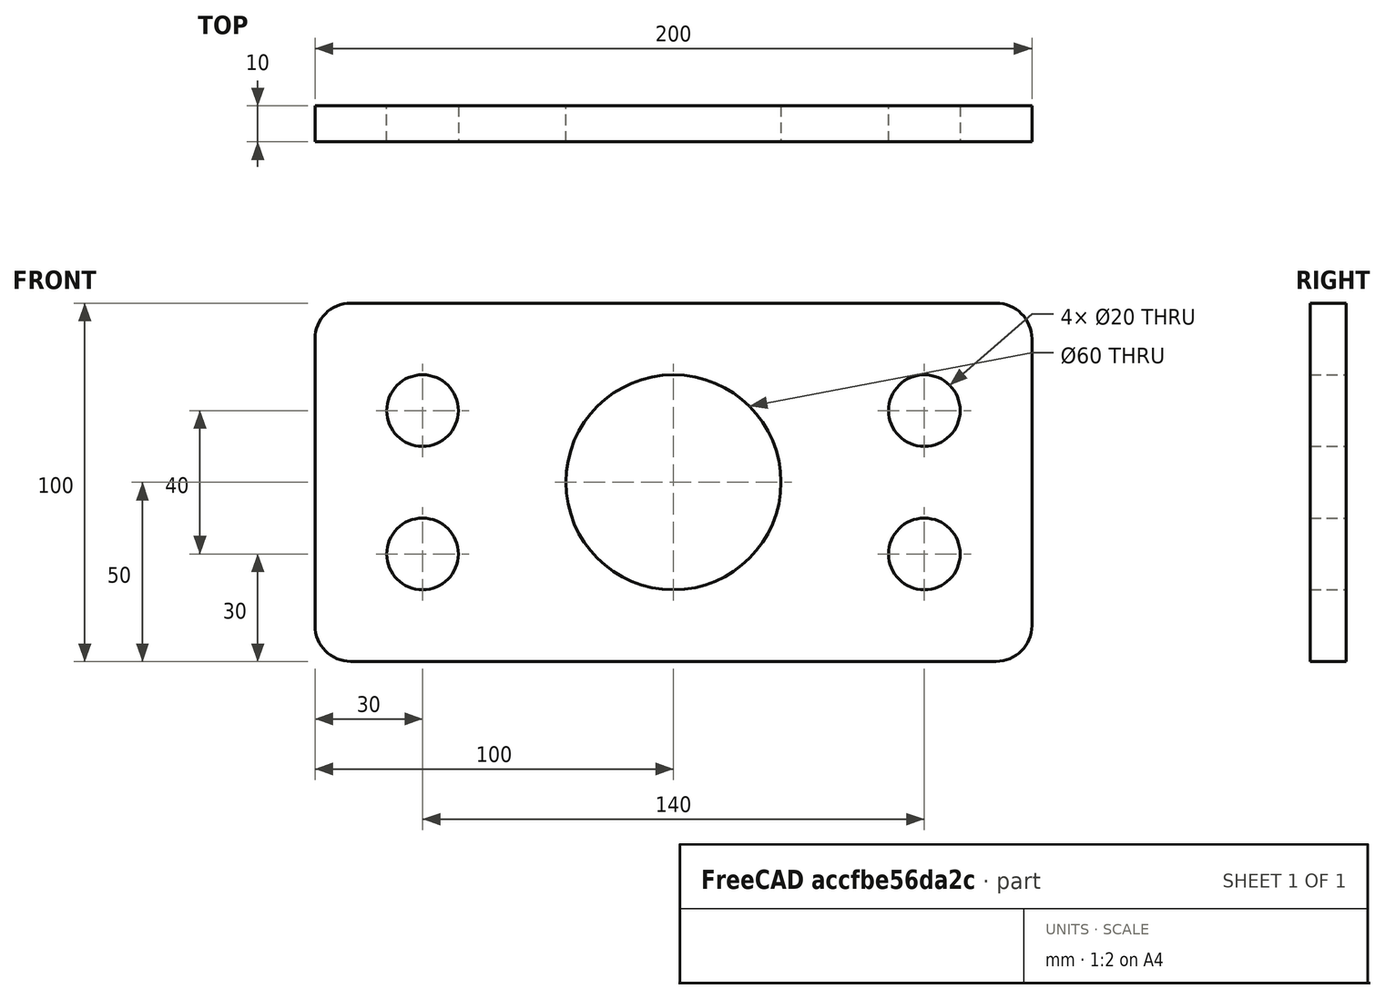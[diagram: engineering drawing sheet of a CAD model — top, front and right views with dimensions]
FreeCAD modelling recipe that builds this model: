
FCSTD DOCUMENT  (FreeCAD 0.18R4 (GitTag))
Label: Assignment-2
License: All rights reserved
LicenseURL: http://en.wikipedia.org/wiki/All_rights_reserved
objects: TechDraw::DrawViewDimension×8, TechDraw::DrawViewAnnotation×4, TechDraw::DrawViewPart×3, PartDesign::Fillet×2, Sketcher::SketchObject×1, PartDesign::Pad×1, PartDesign::Body×1, TechDraw::DrawSVGTemplate×1, TechDraw::DrawPage×1
note: 6 computed .brp shape members not serialized (recipe doc carries the construction recipe); baked Part::Feature solids carry a one-line shape summary decoded from their .brp

FEATURE [Sketcher::SketchObject] Sketch
  MapMode = 5
  Placement = pos=(0,0,0) rot=(1,0,0;1.5708rad)
  Support = -> [XZ_Plane]
  sketch-geometry (9):
    g0: LineSegment StartX=-100 StartY=50 StartZ=0 EndX=100 EndY=50 EndZ=0
    g1: LineSegment StartX=100 StartY=50 StartZ=0 EndX=100 EndY=-50 EndZ=0
    g2: LineSegment StartX=100 StartY=-50 StartZ=0 EndX=-100 EndY=-50 EndZ=0
    g3: LineSegment StartX=-100 StartY=-50 StartZ=0 EndX=-100 EndY=50 EndZ=0
    g4: Circle CenterX=0 CenterY=0 CenterZ=0 NormalX=0 NormalY=0 NormalZ=1 AngleXU=0 Radius=30
    g5: Circle CenterX=-70 CenterY=20 CenterZ=0 NormalX=0 NormalY=0 NormalZ=1 AngleXU=0 Radius=10
    g6: Circle CenterX=70 CenterY=20 CenterZ=0 NormalX=0 NormalY=0 NormalZ=1 AngleXU=0 Radius=10
    g7: Circle CenterX=70 CenterY=-20 CenterZ=0 NormalX=0 NormalY=0 NormalZ=1 AngleXU=0 Radius=10
    g8: Circle CenterX=-70 CenterY=-20 CenterZ=0 NormalX=0 NormalY=0 NormalZ=1 AngleXU=0 Radius=10
  constraints (25):
    c: Coincident(g0,g1)
    c: Coincident(g1,g2)
    c: Coincident(g2,g3)
    c: Coincident(g3,g0)
    c: Horizontal(g0)
    c: Horizontal(g2)
    c: Vertical(g1)
    c: Vertical(g3)
    c: Symmetric(g1,g0,g-1)
    c: DistanceX(g0,g0) = 200
    c: DistanceY(g3,g3) = 100
    c: Diameter(g4) = 60
    c: Coincident(g4,g-1)
    c: Radius(g5) = 10
    c: DistanceY(g-1,g5) = 20
    c: DistanceX(g5,g-1) = 70
    c: Radius(g6) = 10
    c: DistanceY(g-1,g6) = 20
    c: DistanceX(g-1,g6) = 70
    c: Radius(g8) = 10
    c: Radius(g7) = 10
    c: DistanceY(g8,g-1) = 20
    c: DistanceY(g7,g-1) = 20
    c: DistanceX(g8,g-1) = 70
    c: DistanceX(g-1,g7) = 70
FEATURE [PartDesign::Pad] Pad
  Length = 10
  Length2 = 100
  Placement = pos=(0,0,0) rot=(1,0,0;1.5708rad)
  Profile = -> Sketch
  Type = 0
FEATURE [PartDesign::Fillet] Fillet
  Base = -> Pad [Edge5,Edge2,Edge1]
  BaseFeature = -> Pad
  Placement = pos=(0,0,0) rot=(1,0,0;1.5708rad)
  Radius = 10
FEATURE [PartDesign::Fillet] Fillet001
  Base = -> Fillet [Edge29]
  BaseFeature = -> Fillet
  Placement = pos=(0,0,0) rot=(1,0,0;1.5708rad)
  Radius = 10
FEATURE [PartDesign::Body] Body
  Group = -> [Sketch,Pad,Fillet,Fillet001]
  Origin = -> Origin
  Tip = -> Fillet001
FEATURE [TechDraw::DrawSVGTemplate] Template
  EditableTexts = Designed_by_Name=SOUMOJIT SHOME; Drawing_number=Drawing number-01; FC-Date=08/11/2022; FC-SC=1:2; FC-SH=01; FC-Title=Academy of Technology; Subtitle=ECE-3 (X) ROLL-139; Weight=Weight
  Height = 210
  Orientation = 1
  Width = 297
FEATURE [TechDraw::DrawViewPart] View
  CoarseView = false
  Direction = (0,-1,0)
  Focus = 100
  HardHidden = false
  IsoCount = 0
  IsoHidden = false
  IsoVisible = false
  LockPosition = false
  Perspective = false
  Rotation = 0
  Scale = 0.5
  ScaleType = 0
  SeamHidden = false
  SeamVisible = false
  SmoothHidden = false
  SmoothVisible = false
  Source = -> [Fillet001]
  X = 93.3024
  Y = 148.577
FEATURE [TechDraw::DrawViewPart] View001
  CoarseView = false
  Direction = (0,0,1)
  Focus = 100
  HardHidden = false
  IsoCount = 0
  IsoHidden = false
  IsoVisible = false
  LockPosition = true
  Perspective = false
  Rotation = 0
  Scale = 0.5
  ScaleType = 0
  SeamHidden = false
  SeamVisible = false
  SmoothHidden = false
  SmoothVisible = false
  Source = -> [Fillet001]
  X = 79.3389
  Y = 61.8996
FEATURE [TechDraw::DrawViewPart] View002
  CoarseView = false
  Direction = (0.577,-0.577,0.577)
  Focus = 100
  HardHidden = false
  IsoCount = 0
  IsoHidden = false
  IsoVisible = false
  LockPosition = true
  Perspective = false
  Rotation = 0
  Scale = 0.5
  ScaleType = 0
  SeamHidden = false
  SeamVisible = false
  SmoothHidden = false
  SmoothVisible = false
  Source = -> [Fillet001]
  X = 224.449
  Y = 132.806
FEATURE [TechDraw::DrawViewAnnotation] Annotation
  Font = osifont
  LineSpace = 80
  LockPosition = false
  MaxWidth = -1
  Rotation = 0
  ScaleType = 0
  Text = Front View
  TextSize = 5
  TextStyle = 0
  X = 92.6833
  Y = 85.6386
FEATURE [TechDraw::DrawViewAnnotation] Annotation001
  Font = osifont
  LineSpace = 80
  LockPosition = false
  MaxWidth = -1
  Rotation = 0
  ScaleType = 0
  Text = Top View
  TextSize = 5
  TextStyle = 0
  X = 81.751
  Y = 44.9605
FEATURE [TechDraw::DrawViewAnnotation] Annotation002
  Font = osifont
  LineSpace = 80
  LockPosition = false
  MaxWidth = -1
  Rotation = 0
  ScaleType = 0
  Text = Isometric View
  TextSize = 5
  TextStyle = 0
  X = 216.771
  Y = 81.8294
FEATURE [TechDraw::DrawViewDimension] Dimension002
  Arbitrary = false
  FormatSpec = %.2f
  LockPosition = false
  MeasureType = 1
  OverTolerance = 0
  References2D = -> [View]
  Rotation = 0
  ScaleType = 0
  Type = 2
  UnderTolerance = 0
  X = 70.9026
  Y = 8.73322
FEATURE [TechDraw::DrawViewDimension] Dimension003
  Arbitrary = false
  FormatSpec = %.2f
  LockPosition = false
  MeasureType = 1
  OverTolerance = 0
  References2D = -> [View]
  Rotation = 0
  ScaleType = 0
  Type = 2
  UnderTolerance = 0
  X = -68.9054
  Y = 7.09095
FEATURE [TechDraw::DrawViewDimension] Dimension004
  Arbitrary = false
  FormatSpec = %.2f
  LockPosition = true
  MeasureType = 1
  OverTolerance = 0
  References2D = -> [View]
  Rotation = 0
  ScaleType = 0
  Type = 1
  UnderTolerance = 0
  X = -17.6294
  Y = -40.2197
FEATURE [TechDraw::DrawViewDimension] Dimension005
  Arbitrary = false
  FormatSpec = %.2f
  LockPosition = false
  MeasureType = 1
  OverTolerance = 0
  References2D = -> [View]
  Rotation = 0
  ScaleType = 0
  Type = 1
  UnderTolerance = 0
  X = 18.1794
  Y = -50.9505
FEATURE [TechDraw::DrawViewDimension] Dimension006
  Arbitrary = false
  FormatSpec = %.2f
  LockPosition = false
  MeasureType = 1
  OverTolerance = 0
  References2D = -> [View001]
  Rotation = 0
  ScaleType = 0
  Type = 2
  UnderTolerance = 0
  X = 54.8501
  Y = 14.0264
FEATURE [TechDraw::DrawViewAnnotation] Annotation003
  Font = osifont
  LineSpace = 80
  LockPosition = true
  MaxWidth = -1
  Rotation = 0
  ScaleType = 0
  Text = DRILL TEMPLATE
  TextSize = 5
  TextStyle = 0
  X = 211.716
  Y = 31.004
FEATURE [TechDraw::DrawViewDimension] Dimension008
  Arbitrary = false
  FormatSpec = R%.2f
  LockPosition = false
  MeasureType = 1
  OverTolerance = 0
  References2D = -> [View]
  Rotation = 0
  ScaleType = 0
  Type = 4
  UnderTolerance = 0
  X = 49.3874
  Y = 42.747
FEATURE [TechDraw::DrawViewDimension] Dimension
  Arbitrary = false
  FormatSpec = R%.2f
  LockPosition = false
  MeasureType = 1
  OverTolerance = 0
  References2D = -> [View]
  Rotation = 0
  ScaleType = 0
  Type = 4
  UnderTolerance = 0
  X = 75.9486
  Y = 30.2964
FEATURE [TechDraw::DrawViewDimension] Dimension009
  Arbitrary = false
  FormatSpec = R%.2f
  LockPosition = false
  MeasureType = 1
  OverTolerance = 0
  References2D = -> [View]
  Rotation = 0
  ScaleType = 0
  Type = 4
  UnderTolerance = 0
  X = -4.56522
  Y = 39.4269
FEATURE [TechDraw::DrawPage] Page
  KeepUpdated = true
  ProjectionType = 0
  Template = -> Template
  Views = -> [View,View001,View002,Annotation,Annotation001,Annotation002,Dimension002,Dimension003,Dimension004,Dimension005,Dimension006,Annotation003,Dimension008,Dimension,Dimension009]
